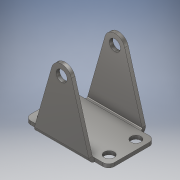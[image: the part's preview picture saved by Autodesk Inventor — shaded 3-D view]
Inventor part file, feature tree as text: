
AUTODESK INVENTOR PART (.ipt)
format: ipt  version: 2018 (Build 220112000, 112)  size: 200,192 bytes
history: native  units: in
note: dims shown in document units (in); Inventor stores cm internally (conversion verified against a paired STEP export)
features: sketch x4, extrude x2, other x2
ambient origin geometry x8: Origin, YZ Plane, XZ Plane, XY Plane, X Axis, Y Axis, Z Axis, Center Point
bodies: Solid1 (feature_tree)
feature tree (8):
  extrude  "Extrusion1"  Depth=1.0in
  extrude  "Extrusion2"  Depth=0.125in
  other  "Bend Part1"
  other  "Bend Part2"
  sketch  "Sketch1"  dims[d0=1.8in d1=1.0in]
  sketch  "Sketch3"  dims[d2=0.075in d3=0.0in d4=0.125in]
  sketch  "Sketch4"  dims[d5=1.4in]
  sketch  "Sketch5"  dims[d6=0.575in d7=0.215in d8=0.215in d9=0.215in d10=0.215in d11=0.6in d12=0.0in d16=1.3in d17=0.6in d18=0.6in d19=0.0in d20=0.22in d21=0.075in d22=0.0in d23=0.24in d24=0.035in d25=90.0deg d26=0.035in d27=90.0deg]
